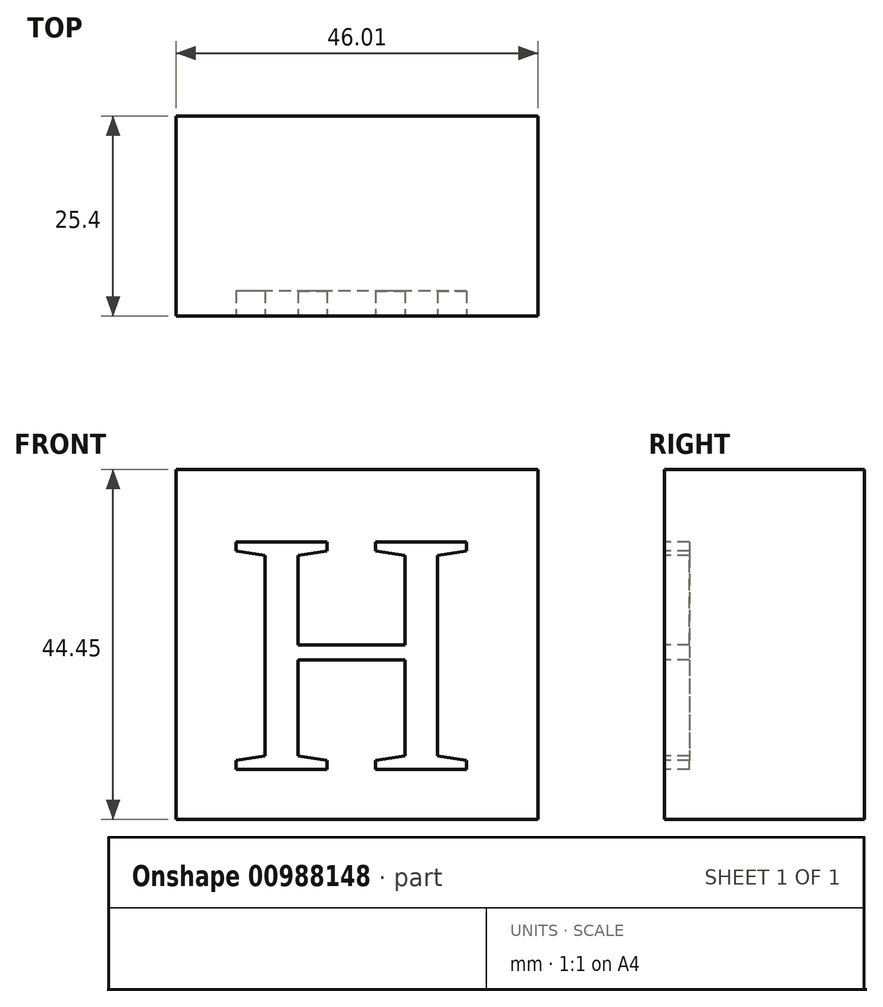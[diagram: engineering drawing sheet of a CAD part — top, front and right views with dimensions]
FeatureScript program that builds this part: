
annotation { "Feature Type Name" : "Feature", "Feature Type Description" : "" }
export const myFeature = defineFeature(function(context is Context, id is Id, definition is map)
    precondition{}
    {
        {
            var Q0;
            Q0=qCreatedBy(makeId("Front.planeOp"),FACE);
            var sketch = newSketch(context, id + "F0", { "sketchPlane" : qUnion([Q0])});
            skText(sketch, "E0", { "text": "H", "fontName": "Tinos-Regular.ttf"});
            const initialGuessF0  = {"E0": [0, 0, 1, 0, 0.03175]};
            skSetInitialGuess(sketch, initialGuessF0);
            skSolve(sketch);
        }
        {
            var Q0;
            Q0=qCreatedBy(makeId("Front.planeOp"),FACE);
            var sketch = newSketch(context, id + "F1", { "sketchPlane" : qUnion([Q0])});
            skLineSegment(sketch, "E1.0", {"start": v(0, 31.75) * mm, "end": v(33.3, 31.75) * mm, "construction": true});
            skLineSegment(sketch, "E2.0", {"start": v(33.3, 0) * mm, "end": v(33.3, 31.75) * mm, "construction": true});
            skLineSegment(sketch, "E3.0", {"start": v(0, 0) * mm, "end": v(0, 31.75) * mm, "construction": true});
            skLineSegment(sketch, "E4.0", {"start": v(0, 0) * mm, "end": v(33.3, 0) * mm, "construction": true});
            skLineSegment(sketch, "E5.0", {"start": v(-6.35, 38.1) * mm, "end": v(39.66, 38.1) * mm});
            skLineSegment(sketch, "E5.1", {"start": v(-6.35, -6.35) * mm, "end": v(-6.35, 38.1) * mm});
            skLineSegment(sketch, "E5.2", {"start": v(-6.35, -6.35) * mm, "end": v(39.66, -6.35) * mm});
            skLineSegment(sketch, "E5.3", {"start": v(39.66, -6.35) * mm, "end": v(39.66, 38.1) * mm});
            skSolve(sketch);
        }
        {
            var Q0;
            Q0 = qSketchRegion(id + "F1", true);
            extrude(context, id + "F2", {"entities" : qUnion([Q0]), "oppositeDirection" : true, "depth" : 25.4 * mm, "offsetDistance" : 25.4 * mm});
        }
        {
            var Q0;
            Q0 = qSketchRegion(id + "F0", true);
            extrude(context, id + "F3", {"entities" : qUnion([Q0]), "operationType" : NewBodyOperationType.REMOVE, "oppositeDirection" : true, "depth" : 3.17 * mm, "offsetDistance" : 25.4 * mm});
        }
    });
